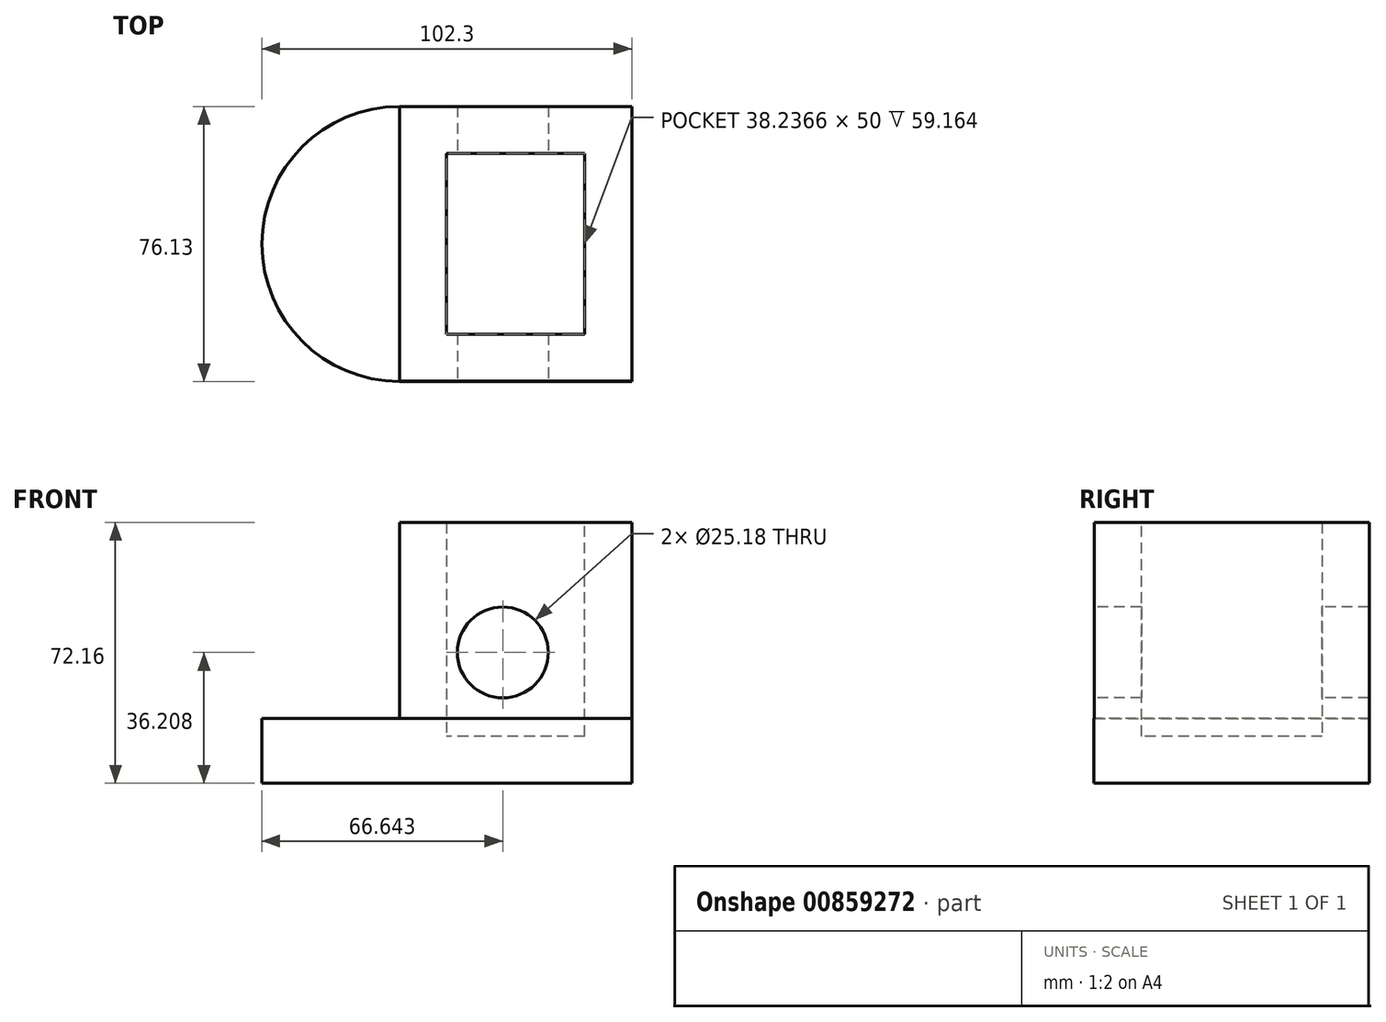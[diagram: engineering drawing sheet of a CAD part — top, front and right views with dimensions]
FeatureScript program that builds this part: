
annotation { "Feature Type Name" : "Feature", "Feature Type Description" : "" }
export const myFeature = defineFeature(function(context is Context, id is Id, definition is map)
    precondition{}
    {
        {
            var Q0;
            Q0=qCreatedBy(makeId("Top.planeOp"),FACE);
            var sketch = newSketch(context, id + "F0", { "sketchPlane" : qUnion([Q0])});
            skLineSegment(sketch, "E0", {"start": v(27.9, 32.24) * mm, "end": v(27.9, -43.89) * mm});
            skLineSegment(sketch, "E1", {"start": v(27.9, -43.89) * mm, "end": v(-36.33, -43.89) * mm});
            skLineSegment(sketch, "E2", {"start": v(27.9, 32.24) * mm, "end": v(-36.33, 32.24) * mm});
            skLineSegment(sketch, "E3", {"start": v(-36.33, 32.24) * mm, "end": v(-36.33, -43.89) * mm});
            skArc(sketch, "E4", {"start": v(-36.33, 32.24) * mm, "mid": v(-74.4, -5.83) * mm, "end": v(-36.33, -43.89) * mm});
            skSolve(sketch);
        }
        {
            var Q0;
            Q0=makeQuery(id+"F0.imprint","IMPRINT",FACE,{"disambiguationData":[TD([[makeQuery(id+"F0.imprint","IMPRINT",EDGE,{"derivedFrom":sQuery(id+"F0.wireOp",EDGE,"E0")}),-1.0]])]});
            var Q1;
            Q1=makeQuery(id+"F0.imprint","IMPRINT",FACE,{"disambiguationData":[TD([[makeQuery(id+"F0.imprint","IMPRINT",EDGE,{"derivedFrom":sQuery(id+"F0.wireOp",EDGE,"E3")}),-1.0]])]});
            extrude(context, id + "F1", {"entities" : qUnion([Q0, Q1]), "depth" : 18 * mm, "offsetDistance" : 25 * mm});
        }
        {
            var Q0;
            Q0=makeQuery(id+"F1.opExtrude","SWEPT_FACE",FACE,{"disambiguationData":[OSD([sQuery(id+"F0.wireOp",EDGE,"E2")])]});
            var sketch = newSketch(context, id + "F2", { "sketchPlane" : qUnion([Q0])});
            skLineSegment(sketch, "E5", {"start": v(-27.9, 18) * mm, "end": v(-27.9, 72.16) * mm});
            skLineSegment(sketch, "E6", {"start": v(-27.9, 72.16) * mm, "end": v(36.33, 72.16) * mm});
            skLineSegment(sketch, "E7", {"start": v(36.33, 72.16) * mm, "end": v(36.33, 18) * mm});
            skSolve(sketch);
        }
        {
            var Q0;
            Q0=makeQuery(id+"F2.imprint","IMPRINT",FACE,{"disambiguationData":[TD([[makeQuery(id+"F2.imprint","IMPRINT",EDGE,{"derivedFrom":sQuery(id+"F2.wireOp",EDGE,"E5")}),-1.0]])]});
            extrude(context, id + "F3", {"entities" : qUnion([Q0]), "operationType" : NewBodyOperationType.ADD, "oppositeDirection" : true, "depth" : 76 * mm, "offsetDistance" : 25 * mm});
        }
        {
            var Q0;
            Q0=makeQuery(id+"F3.opExtrude","CAP_FACE",FACE,{"disambiguationData":[OSD([sQuery(id+"F0.wireOp",EDGE,"E2"),sQuery(id+"F2.wireOp",EDGE,"E5"),sQuery(id+"F2.wireOp",EDGE,"E6"),sQuery(id+"F2.wireOp",EDGE,"E7")])],"isStart":false});
            var sketch = newSketch(context, id + "F4", { "sketchPlane" : qUnion([Q0])});
            skCircle(sketch, "E8", {"center": v(-7.76, 36.2) * mm, "radius": 12.59 * mm});
            skSolve(sketch);
        }
        {
            var Q0;
            Q0=makeQuery(id+"F3.opExtrude","SWEPT_FACE",FACE,{"disambiguationData":[OSD([sQuery(id+"F2.wireOp",EDGE,"E6")])]});
            shell(context, id + "F5", {"entities" : qUnion([Q0]), "thickness" : 13 * mm});
        }
        {
            var Q0;
            Q0=makeQuery(id+"F4.imprint","IMPRINT",FACE,{"disambiguationData":[TD([[makeQuery(id+"F4.imprint","IMPRINT",EDGE,{"derivedFrom":sQuery(id+"F4.wireOp",EDGE,"E8")}),1.0]])]});
            extrude(context, id + "F6", {"entities" : qUnion([Q0]), "operationType" : NewBodyOperationType.REMOVE, "oppositeDirection" : true, "depth" : 205.6 * mm, "offsetDistance" : 25 * mm});
        }
        {
            var Q0;
            Q0=makeQuery(id+"F3.opExtrude","CAP_FACE",FACE,{"disambiguationData":[OSD([sQuery(id+"F0.wireOp",EDGE,"E2"),sQuery(id+"F2.wireOp",EDGE,"E5"),sQuery(id+"F2.wireOp",EDGE,"E6"),sQuery(id+"F2.wireOp",EDGE,"E7")])],"isStart":false});
            cPlane(context, id + "F7", {"entities" : qUnion([Q0]), "cplaneType" : CPlaneType.OFFSET, "offset" : 36 * mm, "oppositeDirection" : true, "width" : 150 * mm, "height" : 150 * mm});
        }
    });
